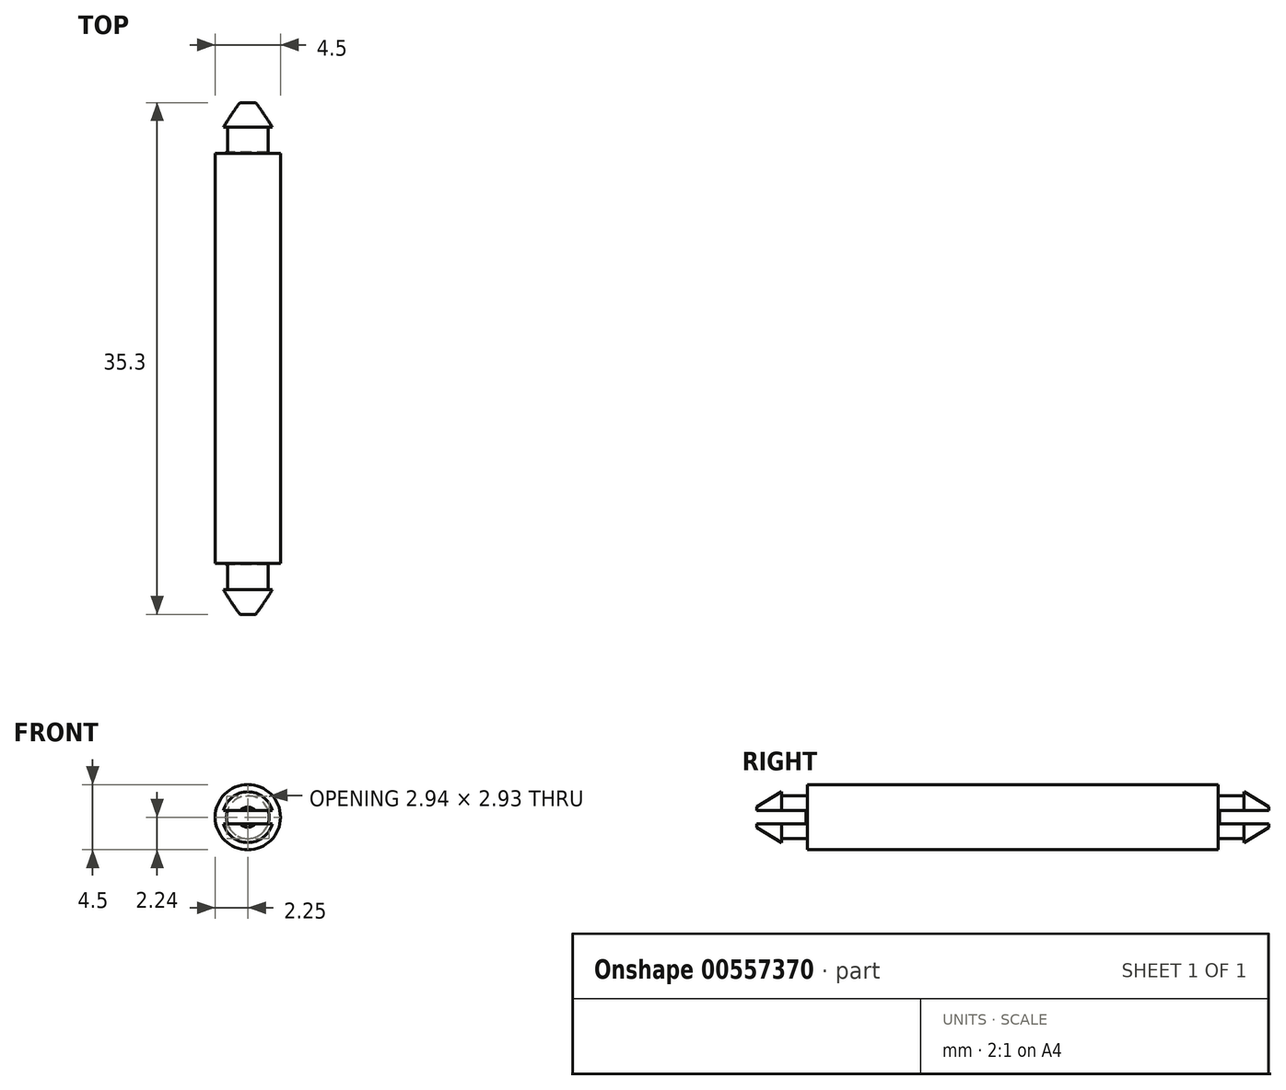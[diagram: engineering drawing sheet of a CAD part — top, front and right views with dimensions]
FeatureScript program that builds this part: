
annotation { "Feature Type Name" : "Feature", "Feature Type Description" : "" }
export const myFeature = defineFeature(function(context is Context, id is Id, definition is map)
    precondition{}
    {
        {
            var Q0;
            Q0=qCreatedBy(makeId("Front.planeOp"),FACE);
            var sketch = newSketch(context, id + "F0", { "sketchPlane" : qUnion([Q0])});
            skCircle(sketch, "E0", {"center": v(0, 0) * mm, "radius": 2.25 * mm});
            skCircle(sketch, "E1", {"center": v(0, 0) * mm, "radius": 1.48 * mm});
            skCircle(sketch, "E2", {"center": v(0, 0) * mm, "radius": 0.7 * mm});
            skSolve(sketch);
        }
        {
            var Q0;
            Q0=makeQuery(id+"F0.imprint","IMPRINT",FACE,{"disambiguationData":[TD([[makeQuery(id+"F0.imprint","IMPRINT",EDGE,{"derivedFrom":sQuery(id+"F0.wireOp",EDGE,"E2")}),1.0]])]});
            extrude(context, id + "F1", {"entities" : qUnion([Q0]), "endBound" : BoundingType.SYMMETRIC, "depth" : 35.3 * mm, "offsetDistance" : 25 * mm});
        }
        {
            var Q0;
            Q0=makeQuery(id+"F0.imprint","IMPRINT",FACE,{"disambiguationData":[TD([[makeQuery(id+"F0.imprint","IMPRINT",EDGE,{"derivedFrom":sQuery(id+"F0.wireOp",EDGE,"E1")}),1.0]])]});
            extrude(context, id + "F2", {"entities" : qUnion([Q0]), "operationType" : NewBodyOperationType.ADD, "endBound" : BoundingType.SYMMETRIC, "depth" : 31.9 * mm, "offsetDistance" : 25 * mm});
        }
        {
            var Q0;
            Q0=makeQuery(id+"F0.imprint","IMPRINT",FACE,{"disambiguationData":[TD([[makeQuery(id+"F0.imprint","IMPRINT",EDGE,{"derivedFrom":sQuery(id+"F0.wireOp",EDGE,"E0")}),1.0]])]});
            extrude(context, id + "F3", {"entities" : qUnion([Q0]), "operationType" : NewBodyOperationType.ADD, "endBound" : BoundingType.SYMMETRIC, "depth" : 28.3 * mm, "offsetDistance" : 25 * mm});
        }
        {
            var Q0;
            Q0=qCreatedBy(makeId("Right.planeOp"),FACE);
            var sketch = newSketch(context, id + "F4", { "sketchPlane" : qUnion([Q0])});
            skLineSegment(sketch, "E3", {"start": v(17.65, 0.7) * mm, "end": v(15.95, 1.75) * mm});
            skLineSegment(sketch, "E4", {"start": v(15.95, 1.75) * mm, "end": v(15.95, 0.7) * mm});
            skLineSegment(sketch, "E5", {"start": v(15.95, 0.7) * mm, "end": v(17.65, 0.7) * mm});
            skLineSegment(sketch, "E6", {"start": v(-15.95, 0.7) * mm, "end": v(-15.95, 1.75) * mm});
            skLineSegment(sketch, "E7", {"start": v(-15.95, 1.75) * mm, "end": v(-17.65, 0.7) * mm});
            skLineSegment(sketch, "E8", {"start": v(-17.65, 0.7) * mm, "end": v(-15.95, 0.7) * mm});
            skSolve(sketch);
        }
        {
            var Q0;
            Q0=makeQuery(id+"F4.imprint","IMPRINT",FACE,{"disambiguationData":[TD([[makeQuery(id+"F4.imprint","IMPRINT",EDGE,{"derivedFrom":sQuery(id+"F4.wireOp",EDGE,"E3")}),1.0]])]});
            var Q1;
            Q1=makeQuery(id+"F4.imprint","IMPRINT",FACE,{"disambiguationData":[TD([[makeQuery(id+"F4.imprint","IMPRINT",EDGE,{"derivedFrom":sQuery(id+"F4.wireOp",EDGE,"E6")}),1.0]])]});
            var Q2;
            Q2=makeQuery(id+"F2.opExtrude","CAP_EDGE",EDGE,{"disambiguationData":[OSD([sQuery(id+"F0.wireOp",EDGE,"E1")])],"isStart":true});
            revolve(context, id + "F5", {"operationType" : NewBodyOperationType.ADD, "entities" : qUnion([Q0, Q1]), "axis" : qUnion([Q2]), "revolveType" : RevolveType.FULL});
        }
        {
            var Q0;
            Q0=makeQuery(id+"F1.opExtrude","CAP_FACE",FACE,{"disambiguationData":[OSD([sQuery(id+"F0.wireOp",EDGE,"E2")])],"isStart":true});
            var sketch = newSketch(context, id + "F6", { "sketchPlane" : qUnion([Q0])});
            skLineSegment(sketch, "E9.bottom", {"start": v(-2.72, 0.45) * mm, "end": v(2.8, 0.45) * mm});
            skLineSegment(sketch, "E9.top", {"start": v(-2.72, -0.45) * mm, "end": v(2.8, -0.45) * mm});
            skLineSegment(sketch, "E9.left", {"start": v(-2.72, 0.45) * mm, "end": v(-2.72, -0.45) * mm});
            skLineSegment(sketch, "E9.right", {"start": v(2.8, 0.45) * mm, "end": v(2.8, -0.45) * mm});
            skPoint(sketch, "E9.middle", {"position": v(0.05, 0) * mm});
            skSolve(sketch);
        }
        {
            var Q0;
            Q0=makeQuery(id+"F1.opExtrude","CAP_FACE",FACE,{"disambiguationData":[OSD([sQuery(id+"F0.wireOp",EDGE,"E2")])],"isStart":false});
            var sketch = newSketch(context, id + "F7", { "sketchPlane" : qUnion([Q0])});
            skLineSegment(sketch, "E10.bottom", {"start": v(2.42, -0.45) * mm, "end": v(-2.42, -0.45) * mm});
            skLineSegment(sketch, "E10.top", {"start": v(2.42, 0.45) * mm, "end": v(-2.42, 0.45) * mm});
            skLineSegment(sketch, "E10.left", {"start": v(2.42, -0.45) * mm, "end": v(2.42, 0.45) * mm});
            skLineSegment(sketch, "E10.right", {"start": v(-2.42, -0.45) * mm, "end": v(-2.42, 0.45) * mm});
            skPoint(sketch, "E10.middle", {"position": v(0, 0) * mm});
            skSolve(sketch);
        }
        {
            var Q0;
            Q0 = qSketchRegion(id + "F6", true);
            extrude(context, id + "F8", {"entities" : qUnion([Q0]), "operationType" : NewBodyOperationType.REMOVE, "oppositeDirection" : true, "depth" : 3.4 * mm, "offsetDistance" : 25 * mm});
        }
        {
            var Q0;
            Q0 = qSketchRegion(id + "F7", true);
            extrude(context, id + "F9", {"entities" : qUnion([Q0]), "operationType" : NewBodyOperationType.REMOVE, "oppositeDirection" : true, "depth" : 3.4 * mm, "offsetDistance" : 25 * mm});
        }
    });
